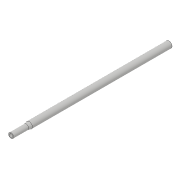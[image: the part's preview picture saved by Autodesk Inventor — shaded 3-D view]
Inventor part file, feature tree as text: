
AUTODESK INVENTOR PART (.ipt)
format: ipt  version: 2018.3 (Build 223284000, 284)  size: 95,232 bytes
history: native  units: in
note: dims shown in document units (in); Inventor stores cm internally (conversion verified against a paired STEP export)
features: sketch x4, extrude x3, revolve x1, projected_geometry x1
ambient origin geometry x8: Origin, YZ Plane, XZ Plane, XY Plane, X Axis, Y Axis, Z Axis, Center Point
bodies: Solid1 (feature_tree)
feature tree (9):
  extrude  "Extrusion1"  Depth=11.125in TaperAngle=0.0deg
  revolve  "Revolution1"  [1 undecoded]
  extrude  "Extrusion2"  TaperAngle=90.0deg  [1 undecoded]
  extrude  "Extrusion3"  Depth=1.44in TaperAngle=0.0deg
  sketch  "Sketch1"  dims[d0=0.51in d1=11.125in d2=0.0in]
  sketch  "Sketch3"  dims[d3=1.44in d4=0.2025in]
  projected_geometry  "Projected Loop1"
  sketch  "Sketch4"  dims[d5=1.2in d6=90.0deg]
  sketch  "Sketch5"  dims[d7=0.291in d8=1.44in d9=0.0in d10=0.406in d11=11.0in d12=0.0in]
note: 2 required parameter values undecoded (feature->parameter linkage not recoverable at this tier; creation-order binding heuristic only, values carry confidence <= 0.55)